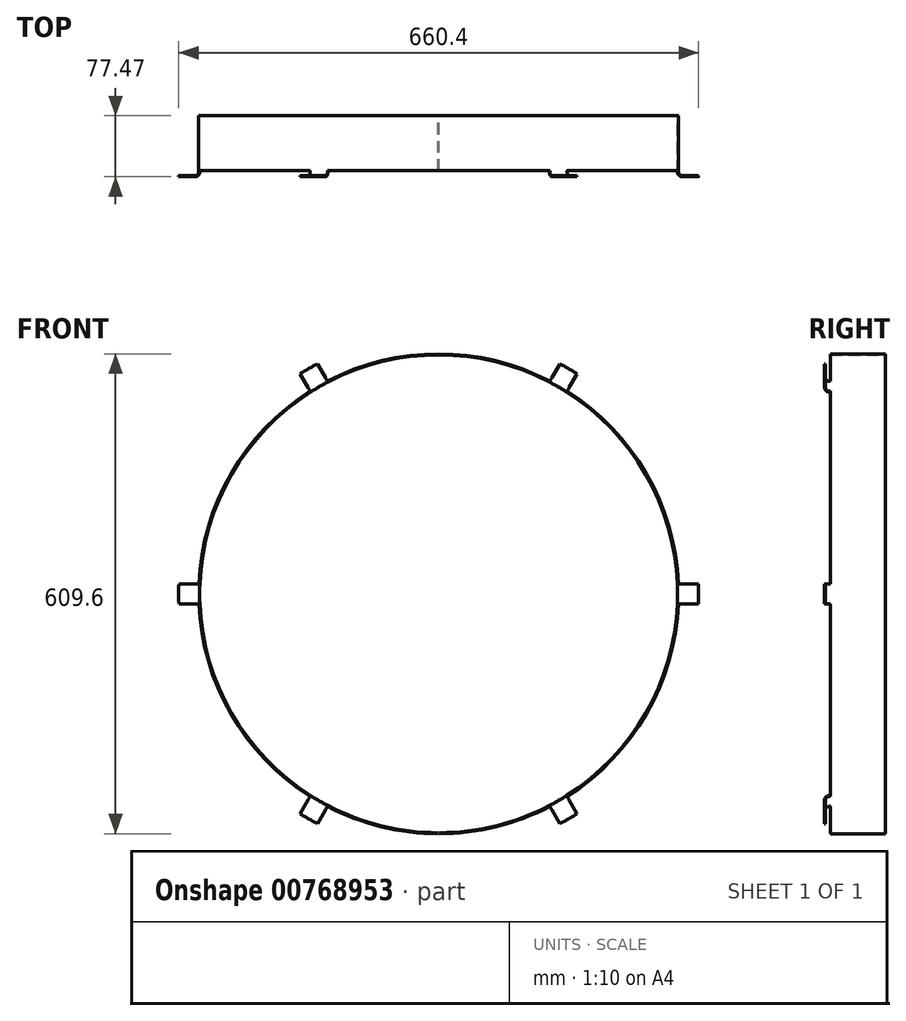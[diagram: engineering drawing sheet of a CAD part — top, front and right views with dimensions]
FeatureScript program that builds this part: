
annotation { "Feature Type Name" : "Feature", "Feature Type Description" : "" }
export const myFeature = defineFeature(function(context is Context, id is Id, definition is map)
    precondition{}
    {
        {
            var Q0;
            Q0=qCreatedBy(makeId("Top.planeOp"),FACE);
            var sketch = newSketch(context, id + "F0", { "sketchPlane" : qUnion([Q0])});
            skLineSegment(sketch, "E0", {"start": v(304.8, 76.2) * mm, "end": v(304.8, 5.08) * mm});
            skLineSegment(sketch, "E1", {"start": v(309.88, 0) * mm, "end": v(330.2, 0) * mm});
            skLineSegment(sketch, "E2", {"start": v(0, 66.91) * mm, "end": v(0, 0) * mm, "construction": true});
            skLineSegment(sketch, "E3.0", {"start": v(309.88, -1.27) * mm, "end": v(330.2, -1.27) * mm});
            skLineSegment(sketch, "E3.1", {"start": v(303.53, 76.2) * mm, "end": v(303.53, 5.08) * mm});
            skLineSegment(sketch, "E4", {"start": v(330.2, -1.27) * mm, "end": v(330.2, 0) * mm});
            skLineSegment(sketch, "E5", {"start": v(303.53, 76.2) * mm, "end": v(304.8, 76.2) * mm});
            skPoint(sketch, "E6.visualSharp", {"position": v(304.8, 0) * mm});
            skArc(sketch, "E6.filletArc", {"start": v(304.8, 5.08) * mm, "mid": v(306.29, 1.49) * mm, "end": v(309.88, 0) * mm});
            skPoint(sketch, "E7.visualSharp", {"position": v(303.53, -1.27) * mm});
            skArc(sketch, "E7.filletArc", {"start": v(303.53, 5.08) * mm, "mid": v(305.39, 0.59) * mm, "end": v(309.88, -1.27) * mm});
            skSolve(sketch);
        }
        {
            var Q0;
            Q0 = qSketchRegion(id + "F0", true);
            var Q1;
            Q1=sQuery(id+"F0.wireOp",EDGE,"E2");
            revolve(context, id + "F1", {"surfaceOperationType" : NewSurfaceOperationType.NEW, "entities" : qUnion([Q0]), "axis" : qUnion([Q1]), "revolveType" : RevolveType.SYMMETRIC, "angle" : 360 * degree});
        }
        {
            var Q0;
            Q0=qCreatedBy(makeId("Front.planeOp"),FACE);
            var sketch = newSketch(context, id + "F2", { "sketchPlane" : qUnion([Q0])});
            skLineSegment(sketch, "E8", {"start": v(154.1, -292.31) * mm, "end": v(176.1, -279.61) * mm});
            skLineSegment(sketch, "E9", {"start": v(137.87, -213.4) * mm, "end": v(176.1, -279.61) * mm});
            skLineSegment(sketch, "E10", {"start": v(115.88, -226.1) * mm, "end": v(154.1, -292.31) * mm});
            skLineSegment(sketch, "E11", {"start": v(165.1, -285.96) * mm, "end": v(0, 0) * mm, "construction": true});
            skLineSegment(sketch, "E12", {"start": v(0, 0) * mm, "end": v(0, -293) * mm, "construction": true});
            skPoint(sketch, "E13.center", {"position": v(0, 0) * mm});
            skLineSegment(sketch, "E14", {"start": v(137.87, -213.4) * mm, "end": v(115.88, -226.1) * mm});
            skLineSegment(sketch, "E15.1.0", {"start": v(253.75, -12.7) * mm, "end": v(330.2, -12.7) * mm});
            skLineSegment(sketch, "E15.1.1", {"start": v(253.75, 12.7) * mm, "end": v(253.75, -12.7) * mm});
            skLineSegment(sketch, "E15.1.2", {"start": v(253.75, 12.7) * mm, "end": v(330.2, 12.7) * mm});
            skLineSegment(sketch, "E15.1.3", {"start": v(330.2, -12.7) * mm, "end": v(330.2, 12.7) * mm});
            skLineSegment(sketch, "E15.2.0", {"start": v(137.87, 213.4) * mm, "end": v(176.1, 279.61) * mm});
            skLineSegment(sketch, "E15.2.1", {"start": v(115.88, 226.1) * mm, "end": v(137.87, 213.4) * mm});
            skLineSegment(sketch, "E15.2.2", {"start": v(115.88, 226.1) * mm, "end": v(154.1, 292.31) * mm});
            skLineSegment(sketch, "E15.2.3", {"start": v(176.1, 279.61) * mm, "end": v(154.1, 292.31) * mm});
            skLineSegment(sketch, "E15.3.0", {"start": v(-115.88, 226.1) * mm, "end": v(-154.1, 292.31) * mm});
            skLineSegment(sketch, "E15.3.1", {"start": v(-137.87, 213.4) * mm, "end": v(-115.88, 226.1) * mm});
            skLineSegment(sketch, "E15.3.2", {"start": v(-137.87, 213.4) * mm, "end": v(-176.1, 279.61) * mm});
            skLineSegment(sketch, "E15.3.3", {"start": v(-154.1, 292.31) * mm, "end": v(-176.1, 279.61) * mm});
            skLineSegment(sketch, "E15.4.0", {"start": v(-253.75, 12.7) * mm, "end": v(-330.2, 12.7) * mm});
            skLineSegment(sketch, "E15.4.1", {"start": v(-253.75, -12.7) * mm, "end": v(-253.75, 12.7) * mm});
            skLineSegment(sketch, "E15.4.2", {"start": v(-253.75, -12.7) * mm, "end": v(-330.2, -12.7) * mm});
            skLineSegment(sketch, "E15.4.3", {"start": v(-330.2, 12.7) * mm, "end": v(-330.2, -12.7) * mm});
            skLineSegment(sketch, "E15.5.0", {"start": v(-137.87, -213.4) * mm, "end": v(-176.1, -279.61) * mm});
            skLineSegment(sketch, "E15.5.1", {"start": v(-115.88, -226.1) * mm, "end": v(-137.87, -213.4) * mm});
            skLineSegment(sketch, "E15.5.2", {"start": v(-115.88, -226.1) * mm, "end": v(-154.1, -292.31) * mm});
            skLineSegment(sketch, "E15.5.3", {"start": v(-176.1, -279.61) * mm, "end": v(-154.1, -292.31) * mm});
            skCircle(sketch, "E16.0", {"center": v(0, 0) * mm, "radius": 303.53 * mm});
            skCircle(sketch, "E16.1", {"center": v(0, 0) * mm, "radius": 330.2 * mm});
            skSolve(sketch);
        }
        {
            var Q0;
            {var subQ0=sQuery(id+"F2.wireOp",EDGE,"E16.1");var subQ1=sQuery(id+"F2.wireOp",EDGE,"E9");var subQ2=makeQuery(id+"F2.imprint","INTERSECT",VERTEX,{"derivedFrom":[subQ1,subQ0]});Q0=makeQuery(id+"F2.imprint","IMPRINT",FACE,{"disambiguationData":[TD([[makeQuery(id+"F2.imprint","IMPRINT",EDGE,{"disambiguationData":[TD([[subQ2,1.0]])],"derivedFrom":subQ1}),1.0]])]});}
            var Q1;
            {var subQ0=sQuery(id+"F2.wireOp",EDGE,"E16.1");var subQ1=sQuery(id+"F2.wireOp",EDGE,"E15.1.2");var subQ2=makeQuery(id+"F2.imprint","INTERSECT",VERTEX,{"derivedFrom":[subQ1,subQ0]});Q1=makeQuery(id+"F2.imprint","IMPRINT",FACE,{"disambiguationData":[TD([[makeQuery(id+"F2.imprint","IMPRINT",EDGE,{"disambiguationData":[TD([[subQ2,1.0]])],"derivedFrom":subQ1}),1.0]])]});}
            var Q2;
            {var subQ0=sQuery(id+"F2.wireOp",EDGE,"E16.1");var subQ1=sQuery(id+"F2.wireOp",EDGE,"E15.2.2");var subQ2=makeQuery(id+"F2.imprint","INTERSECT",VERTEX,{"derivedFrom":[subQ1,subQ0]});Q2=makeQuery(id+"F2.imprint","IMPRINT",FACE,{"disambiguationData":[TD([[makeQuery(id+"F2.imprint","IMPRINT",EDGE,{"disambiguationData":[TD([[subQ2,1.0]])],"derivedFrom":subQ1}),1.0]])]});}
            var Q3;
            {var subQ0=sQuery(id+"F2.wireOp",EDGE,"E16.1");var subQ1=sQuery(id+"F2.wireOp",EDGE,"E15.3.2");var subQ2=makeQuery(id+"F2.imprint","INTERSECT",VERTEX,{"derivedFrom":[subQ1,subQ0]});Q3=makeQuery(id+"F2.imprint","IMPRINT",FACE,{"disambiguationData":[TD([[makeQuery(id+"F2.imprint","IMPRINT",EDGE,{"disambiguationData":[TD([[subQ2,1.0]])],"derivedFrom":subQ1}),1.0]])]});}
            var Q4;
            {var subQ0=sQuery(id+"F2.wireOp",EDGE,"E16.1");var subQ1=sQuery(id+"F2.wireOp",EDGE,"E15.4.2");var subQ2=makeQuery(id+"F2.imprint","INTERSECT",VERTEX,{"derivedFrom":[subQ1,subQ0]});Q4=makeQuery(id+"F2.imprint","IMPRINT",FACE,{"disambiguationData":[TD([[makeQuery(id+"F2.imprint","IMPRINT",EDGE,{"disambiguationData":[TD([[subQ2,1.0]])],"derivedFrom":subQ1}),1.0]])]});}
            var Q5;
            {var subQ0=sQuery(id+"F2.wireOp",EDGE,"E16.1");var subQ1=sQuery(id+"F2.wireOp",EDGE,"E10");var subQ2=makeQuery(id+"F2.imprint","INTERSECT",VERTEX,{"derivedFrom":[subQ1,subQ0]});Q5=makeQuery(id+"F2.imprint","IMPRINT",FACE,{"disambiguationData":[TD([[makeQuery(id+"F2.imprint","IMPRINT",EDGE,{"disambiguationData":[TD([[subQ2,1.0]])],"derivedFrom":subQ1}),-1.0]])]});}
            extrude(context, id + "F3", {"entities" : qUnion([Q0, Q1, Q2, Q3, Q4, Q5]), "operationType" : NewBodyOperationType.REMOVE, "oppositeDirection" : true, "depth" : 6.35 * mm, "offsetDistance" : 25.4 * mm, "hasSecondDirection" : true, "secondDirectionBound" : SecondDirectionBoundingType.THROUGH_ALL, "secondDirectionOppositeDirection" : false, "secondDirectionDepth" : 25.4 * mm});
        }
        {
            var Q0;
            Q0=qCreatedBy(makeId("Front.planeOp"),FACE);
            var sketch = newSketch(context, id + "F4", { "sketchPlane" : qUnion([Q0])});
            skLineSegment(sketch, "E17.bottom", {"start": v(-0.64, -281.87) * mm, "end": v(0.63, -281.87) * mm});
            skLineSegment(sketch, "E17.top", {"start": v(-0.64, -358.07) * mm, "end": v(0.63, -358.07) * mm});
            skLineSegment(sketch, "E17.left", {"start": v(-0.64, -281.87) * mm, "end": v(-0.64, -358.07) * mm});
            skLineSegment(sketch, "E17.right", {"start": v(0.63, -281.87) * mm, "end": v(0.63, -358.07) * mm});
            skPoint(sketch, "E17.middle", {"position": v(0, -319.97) * mm});
            skSolve(sketch);
        }
        {
            var Q0;
            Q0 = qSketchRegion(id + "F4", true);
            extrude(context, id + "F5", {"entities" : qUnion([Q0]), "operationType" : NewBodyOperationType.REMOVE, "endBound" : BoundingType.THROUGH_ALL, "oppositeDirection" : true, "depth" : 25.4 * mm, "offsetDistance" : 25.4 * mm, "hasSecondDirection" : true, "secondDirectionBound" : SecondDirectionBoundingType.THROUGH_ALL, "secondDirectionOppositeDirection" : false, "secondDirectionDepth" : 25.4 * mm});
        }
    });
